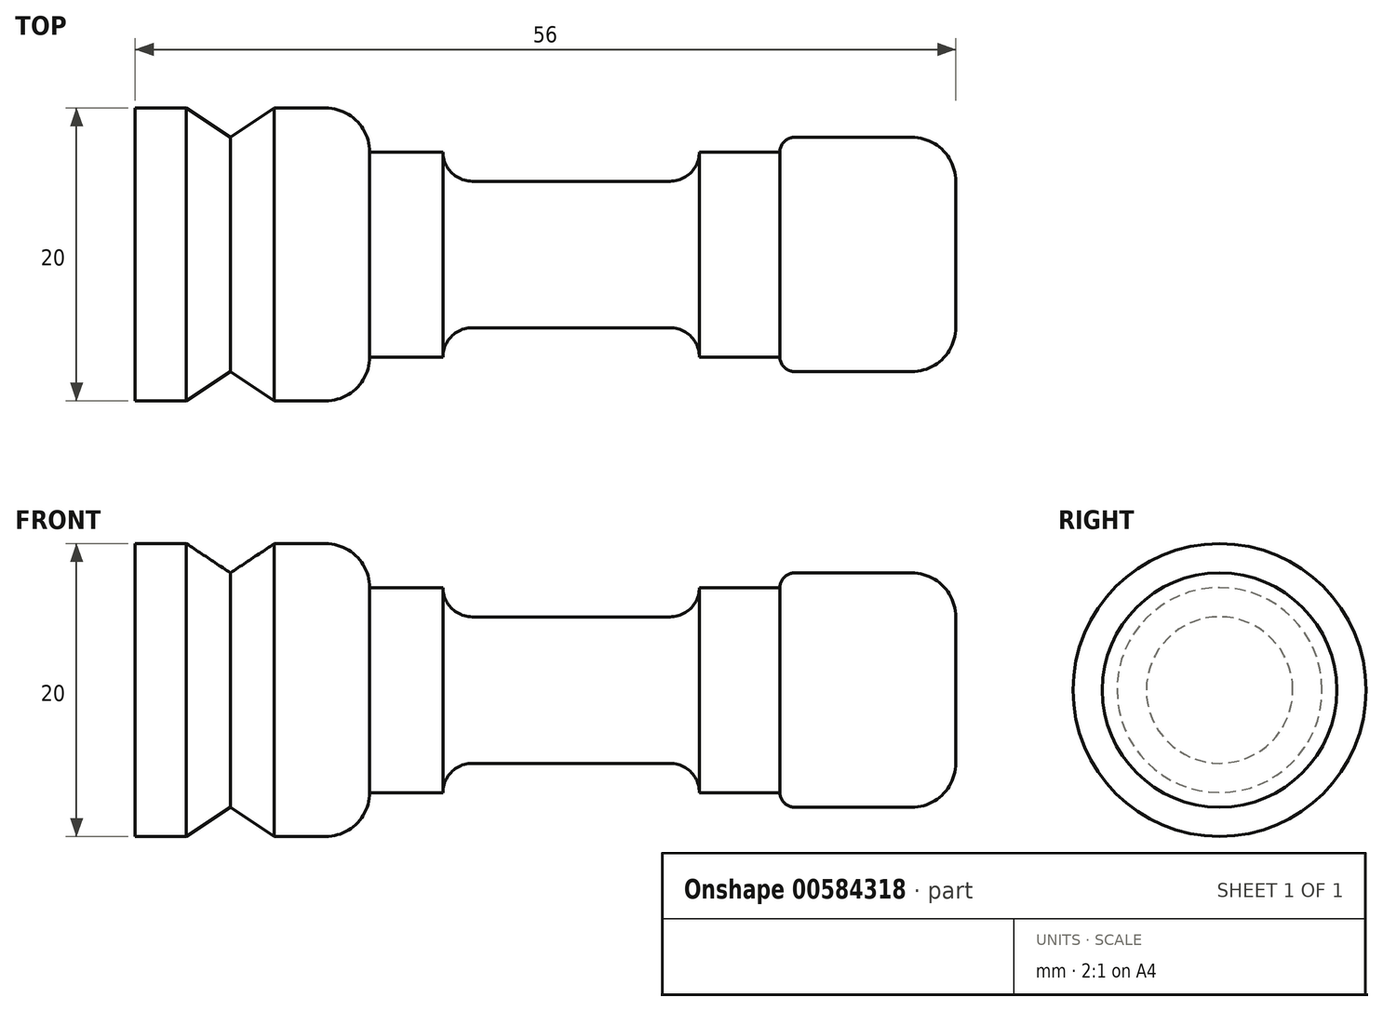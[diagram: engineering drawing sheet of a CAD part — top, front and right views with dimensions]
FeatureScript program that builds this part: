
annotation { "Feature Type Name" : "Feature", "Feature Type Description" : "" }
export const myFeature = defineFeature(function(context is Context, id is Id, definition is map)
    precondition{}
    {
        {
            var Q0;
            Q0=qCreatedBy(makeId("Front.planeOp"),FACE);
            var sketch = newSketch(context, id + "F0", { "sketchPlane" : qUnion([Q0])});
            skLineSegment(sketch, "E0", {"start": v(-23.32, 0) * mm, "end": v(32.68, 0) * mm});
            skLineSegment(sketch, "E1", {"start": v(-23.32, 0) * mm, "end": v(-23.32, -10) * mm});
            skLineSegment(sketch, "E2", {"start": v(-23.32, -10) * mm, "end": v(-19.82, -10) * mm});
            skLineSegment(sketch, "E3", {"start": v(-19.82, -10) * mm, "end": v(-19.82, 0) * mm});
            skLineSegment(sketch, "E4", {"start": v(-13.82, -10) * mm, "end": v(-13.82, 0) * mm});
            skLineSegment(sketch, "E5", {"start": v(-19.82, -10) * mm, "end": v(-16.82, -8) * mm});
            skLineSegment(sketch, "E6", {"start": v(-16.82, -8) * mm, "end": v(-16.82, 0) * mm});
            skLineSegment(sketch, "E7", {"start": v(-13.82, -10) * mm, "end": v(-16.82, -8) * mm});
            skLineSegment(sketch, "E8.trimOffspring", {"start": v(-13.82, -10) * mm, "end": v(-10.32, -10) * mm});
            skLineSegment(sketch, "E9", {"start": v(-7.32, -7) * mm, "end": v(-7.32, 0) * mm});
            skArc(sketch, "E10.filletArc", {"start": v(-10.32, -10) * mm, "mid": v(-8.2, -9.12) * mm, "end": v(-7.32, -7) * mm});
            skLineSegment(sketch, "E11", {"start": v(15.18, -7) * mm, "end": v(15.18, -7) * mm});
            skLineSegment(sketch, "E12", {"start": v(-2.32, -7) * mm, "end": v(-7.32, -7) * mm});
            skLineSegment(sketch, "E13", {"start": v(-2.32, -7) * mm, "end": v(-2.32, -7) * mm});
            skLineSegment(sketch, "E14", {"start": v(-0.32, -5) * mm, "end": v(13.18, -5) * mm});
            skLineSegment(sketch, "E15", {"start": v(32.68, 0) * mm, "end": v(32.68, -5) * mm});
            skLineSegment(sketch, "E16", {"start": v(29.68, -8) * mm, "end": v(21.68, -8) * mm});
            skLineSegment(sketch, "E17", {"start": v(20.68, -7) * mm, "end": v(20.68, 0) * mm});
            skLineSegment(sketch, "E18", {"start": v(15.18, -7) * mm, "end": v(20.68, -7) * mm});
            skPoint(sketch, "E19.visualSharp", {"position": v(32.68, -8) * mm});
            skArc(sketch, "E19.filletArc", {"start": v(29.68, -8) * mm, "mid": v(31.8, -7.12) * mm, "end": v(32.68, -5) * mm});
            skPoint(sketch, "E20.visualSharp", {"position": v(20.68, -8) * mm});
            skArc(sketch, "E20.filletArc", {"start": v(20.68, -7) * mm, "mid": v(20.97, -7.7) * mm, "end": v(21.68, -8) * mm});
            skPoint(sketch, "E21.newPointB", {"position": v(-2.32, 0) * mm});
            skArc(sketch, "E21.filletArc", {"start": v(-0.32, -5) * mm, "mid": v(-1.74, -5.59) * mm, "end": v(-2.32, -7) * mm});
            skPoint(sketch, "E22.newPointA", {"position": v(15.18, 0) * mm});
            skArc(sketch, "E22.filletArc", {"start": v(15.18, -7) * mm, "mid": v(14.6, -5.59) * mm, "end": v(13.18, -5) * mm});
            skLineSegment(sketch, "E23", {"start": v(-33.28, 0) * mm, "end": v(44.59, 0) * mm, "construction": true});
            skSolve(sketch);
        }
        {
            var Q0;
            {var subQ0=sQuery(id+"F0.wireOp",EDGE,"E9");Q0=makeQuery(id+"F0.imprint","IMPRINT",FACE,{"disambiguationData":[TD([[makeQuery(id+"F0.imprint","IMPRINT",EDGE,{"derivedFrom":subQ0}),-1.0]])]});}
            var Q1;
            {var subQ0=sQuery(id+"F0.wireOp",EDGE,"E15");Q1=makeQuery(id+"F0.imprint","IMPRINT",FACE,{"disambiguationData":[TD([[makeQuery(id+"F0.imprint","IMPRINT",EDGE,{"derivedFrom":subQ0}),-1.0]])]});}
            var Q2;
            {var subQ0=sQuery(id+"F0.wireOp",EDGE,"E3");Q2=makeQuery(id+"F0.imprint","IMPRINT",FACE,{"disambiguationData":[TD([[makeQuery(id+"F0.imprint","IMPRINT",EDGE,{"derivedFrom":subQ0}),-1.0]])]});}
            var Q3;
            {var subQ0=sQuery(id+"F0.wireOp",EDGE,"E1");Q3=makeQuery(id+"F0.imprint","IMPRINT",FACE,{"disambiguationData":[TD([[makeQuery(id+"F0.imprint","IMPRINT",EDGE,{"derivedFrom":subQ0}),1.0]])]});}
            var Q4;
            {var subQ1=sQuery(id+"F0.wireOp",EDGE,"E4");Q4=makeQuery(id+"F0.imprint","IMPRINT",FACE,{"disambiguationData":[TD([[makeQuery(id+"F0.imprint","IMPRINT",EDGE,{"derivedFrom":subQ1}),-1.0]])]});}
            var Q5;
            {var subQ0=sQuery(id+"F0.wireOp",EDGE,"E4");Q5=makeQuery(id+"F0.imprint","IMPRINT",FACE,{"disambiguationData":[TD([[makeQuery(id+"F0.imprint","IMPRINT",EDGE,{"derivedFrom":subQ0}),1.0]])]});}
            var Q6;
            Q6=sQuery(id+"F0.wireOp",EDGE,"E23");
            revolve(context, id + "F1", {"entities" : qUnion([Q0, Q1, Q2, Q3, Q4, Q5]), "axis" : qUnion([Q6]), "revolveType" : RevolveType.FULL});
        }
    });
